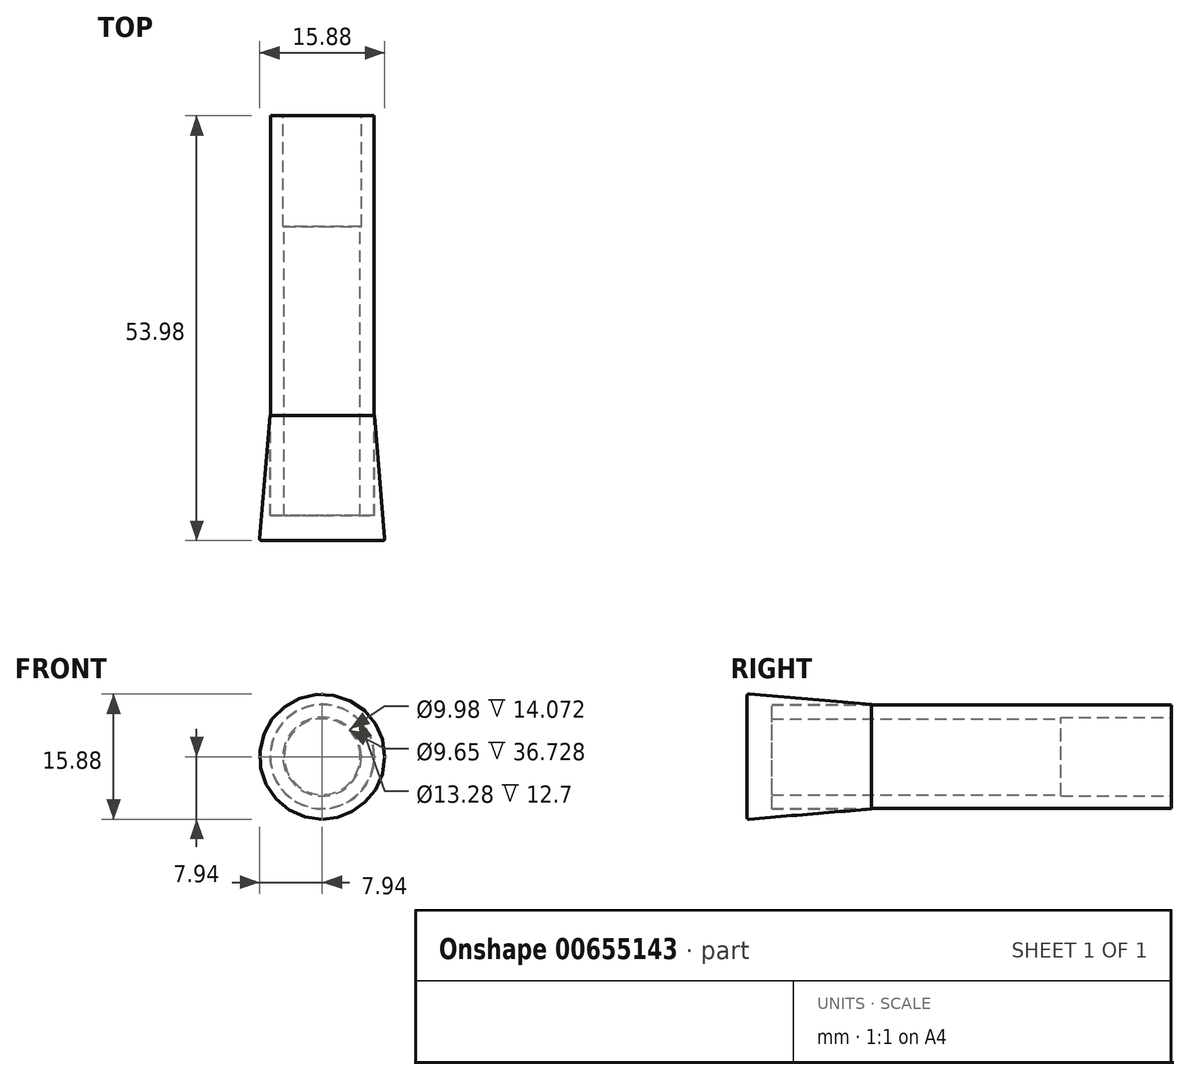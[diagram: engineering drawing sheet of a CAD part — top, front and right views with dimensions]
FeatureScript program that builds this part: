
annotation { "Feature Type Name" : "Feature", "Feature Type Description" : "" }
export const myFeature = defineFeature(function(context is Context, id is Id, definition is map)
    precondition{}
    {
        {
            var Q0;
            Q0=qCreatedBy(makeId("Front.planeOp"),FACE);
            var sketch = newSketch(context, id + "F0", { "sketchPlane" : qUnion([Q0])});
            skCircle(sketch, "E0", {"center": v(0, 0) * mm, "radius": 6.58 * mm});
            skCircle(sketch, "E1", {"center": v(0, 0) * mm, "radius": 5 * mm});
            skSolve(sketch);
        }
        {
            var Q0;
            Q0=makeQuery(id+"F0.imprint","IMPRINT",FACE,{"disambiguationData":[TD([[makeQuery(id+"F0.imprint","IMPRINT",EDGE,{"derivedFrom":sQuery(id+"F0.wireOp",EDGE,"E0")}),1.0]])]});
            extrude(context, id + "F1", {"entities" : qUnion([Q0]), "depth" : 14.07 * mm, "offsetDistance" : 25.4 * mm});
        }
        {
            var Q0;
            Q0=qCreatedBy(makeId("Front.planeOp"),FACE);
            var sketch = newSketch(context, id + "F2", { "sketchPlane" : qUnion([Q0])});
            skCircle(sketch, "E2", {"center": v(0, 0) * mm, "radius": 6.58 * mm});
            skCircle(sketch, "E3", {"center": v(0, 0) * mm, "radius": 4.83 * mm});
            skSolve(sketch);
        }
        {
            var Q0;
            Q0=qSketchRegion(id+"F2",true);
            extrude(context, id + "F3", {"entities" : qUnion([Q0]), "operationType" : NewBodyOperationType.ADD, "depth" : 50.8 * mm, "offsetDistance" : 25.4 * mm, "hasSecondDirection" : true, "secondDirectionOppositeDirection" : false, "secondDirectionDepth" : 14.07 * mm});
        }
        {
            var Q0;
            Q0=qCreatedBy(makeId("Front.planeOp"),FACE);
            var sketch = newSketch(context, id + "F4", { "sketchPlane" : qUnion([Q0])});
            skCircle(sketch, "E4", {"center": v(0, 0) * mm, "radius": 8.23 * mm});
            skCircle(sketch, "E5", {"center": v(0, 0) * mm, "radius": 6.64 * mm});
            skSolve(sketch);
        }
        {
            var Q0;
            Q0=qSketchRegion(id+"F4",true);
            extrude(context, id + "F5", {"entities" : qUnion([Q0]), "depth" : 50.8 * mm, "offsetDistance" : 25.4 * mm, "hasSecondDirection" : true, "secondDirectionOppositeDirection" : false, "secondDirectionDepth" : 38.1 * mm});
        }
        {
            var Q0;
            Q0=qCreatedBy(makeId("Front.planeOp"),FACE);
            var sketch = newSketch(context, id + "F6", { "sketchPlane" : qUnion([Q0])});
            skCircle(sketch, "E6", {"center": v(0, 0) * mm, "radius": 8.23 * mm});
            skSolve(sketch);
        }
        {
            var Q0;
            Q0=qSketchRegion(id+"F6",true);
            extrude(context, id + "F7", {"entities" : qUnion([Q0]), "operationType" : NewBodyOperationType.ADD, "depth" : 53.97 * mm, "offsetDistance" : 25.4 * mm, "hasSecondDirection" : true, "secondDirectionOppositeDirection" : false, "secondDirectionDepth" : 50.8 * mm});
        }
        {
            var Q0;
            Q0=makeQuery(id+"F5.opExtrude","CAP_EDGE",EDGE,{"disambiguationData":[OSD([sQuery(id+"F4.wireOp",EDGE,"E4")])],"isStart":true});
            chamfer(context, id + "F8", {"entities" : qUnion([Q0]), "chamferType" : ChamferType.TWO_OFFSETS, "width1" : 19.05 * mm, "oppositeDirection" : false, "width2" : 1.59 * mm, "tangentPropagation" : true});
        }
        {
            var Q0;
            Q0=makeQuery(id+"F7.opExtrude","CAP_FACE",FACE,{"disambiguationData":[OSD([sQuery(id+"F6.wireOp",EDGE,"E6")])],"isStart":false});
            fillet(context, id + "F9", {"entities" : qUnion([Q0]), "radius" : 0.25 * mm, "tangentPropagation" : true, "allowEdgeOverflow" : false});
        }
    });
